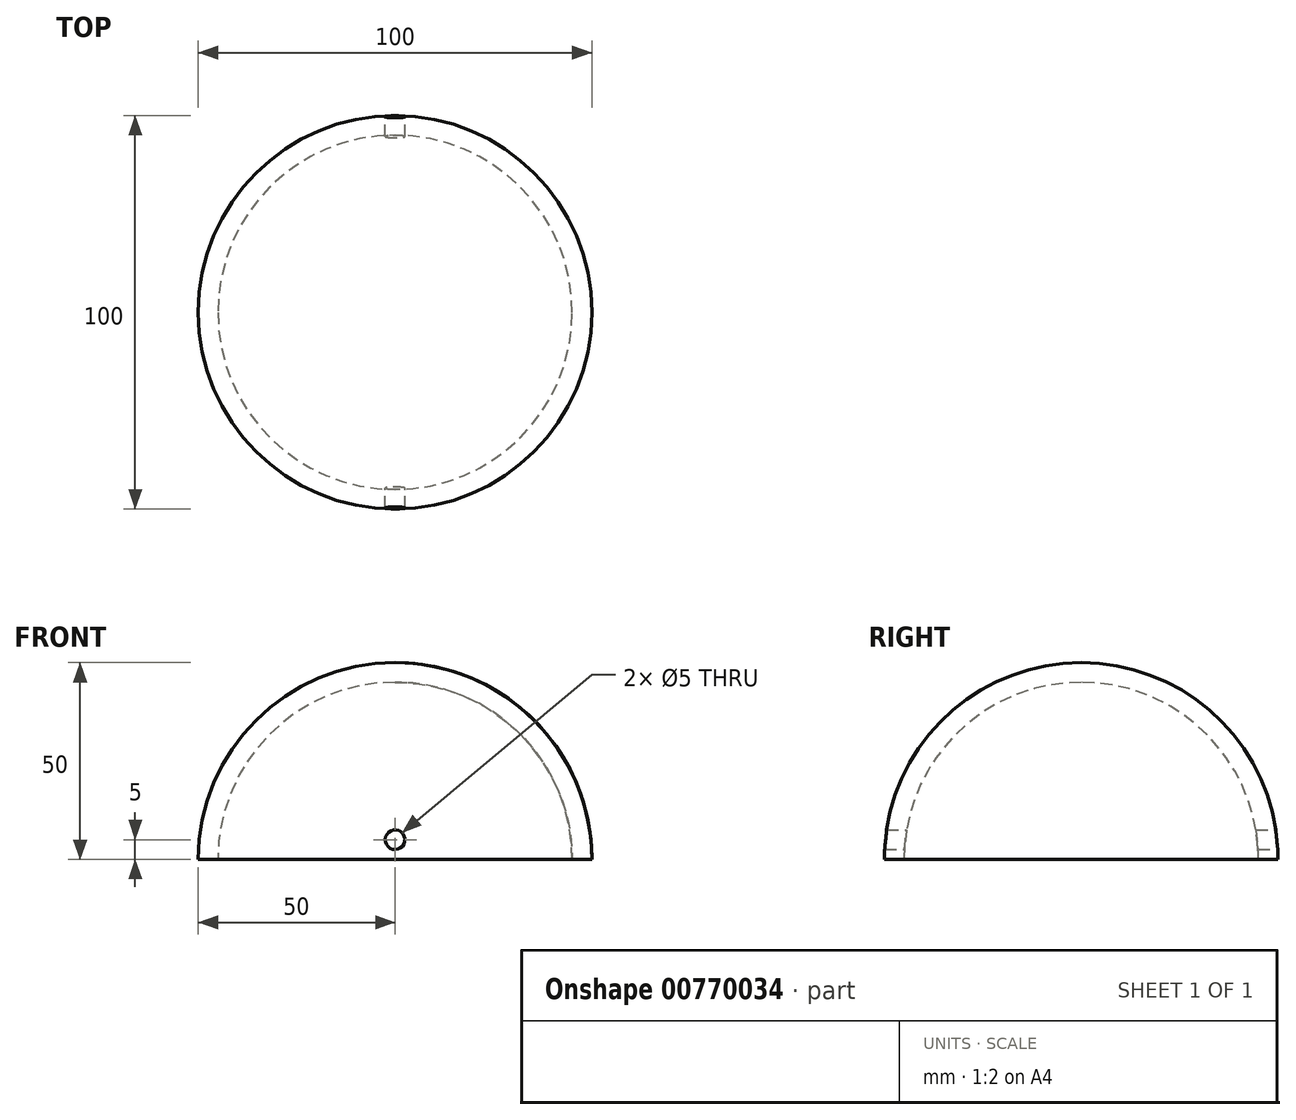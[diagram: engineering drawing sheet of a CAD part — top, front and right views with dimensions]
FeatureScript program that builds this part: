
annotation { "Feature Type Name" : "Feature", "Feature Type Description" : "" }
export const myFeature = defineFeature(function(context is Context, id is Id, definition is map)
    precondition{}
    {
        {
            var Q0;
            Q0=qCreatedBy(makeId("Front.planeOp"),FACE);
            var sketch = newSketch(context, id + "F0", { "sketchPlane" : qUnion([Q0])});
            skArc(sketch, "E0", {"start": v(0, 50) * mm, "mid": v(-35.36, 35.36) * mm, "end": v(-50, 0) * mm});
            skArc(sketch, "E1", {"start": v(0, 45) * mm, "mid": v(-31.82, 31.82) * mm, "end": v(-45, 0) * mm});
            skLineSegment(sketch, "E2", {"start": v(-50, 0) * mm, "end": v(-45, 0) * mm});
            skLineSegment(sketch, "E3", {"start": v(0, 45) * mm, "end": v(0, 50) * mm});
            skSolve(sketch);
        }
        {
            var Q0;
            Q0=makeQuery(id+"F0.imprint","IMPRINT",FACE,{"disambiguationData":[TD([[makeQuery(id+"F0.imprint","IMPRINT",EDGE,{"derivedFrom":sQuery(id+"F0.wireOp",EDGE,"E0")}),1.0]])]});
            var Q1;
            Q1=sQuery(id+"F0.wireOp",EDGE,"E3");
            revolve(context, id + "F1", {"surfaceOperationType" : NewSurfaceOperationType.NEW, "entities" : qUnion([Q0]), "axis" : qUnion([Q1]), "revolveType" : RevolveType.FULL});
        }
        {
            var Q0;
            Q0=qCreatedBy(makeId("Front.planeOp"),FACE);
            var sketch = newSketch(context, id + "F2", { "sketchPlane" : qUnion([Q0])});
            skCircle(sketch, "E4", {"center": v(0, 5) * mm, "radius": 2.5 * mm});
            skSolve(sketch);
        }
        {
            var Q0;
            Q0=makeQuery(id+"F2.imprint","IMPRINT",FACE,{"disambiguationData":[TD([[makeQuery(id+"F2.imprint","IMPRINT",EDGE,{"derivedFrom":sQuery(id+"F2.wireOp",EDGE,"E4")}),1.0]])]});
            extrude(context, id + "F3", {"entities" : qUnion([Q0]), "operationType" : NewBodyOperationType.REMOVE, "endBound" : BoundingType.SYMMETRIC, "depth" : 100 * mm, "offsetDistance" : 25 * mm, "hasSecondDirection" : true, "secondDirectionOppositeDirection" : true, "secondDirectionDepth" : 25 * mm});
        }
    });
